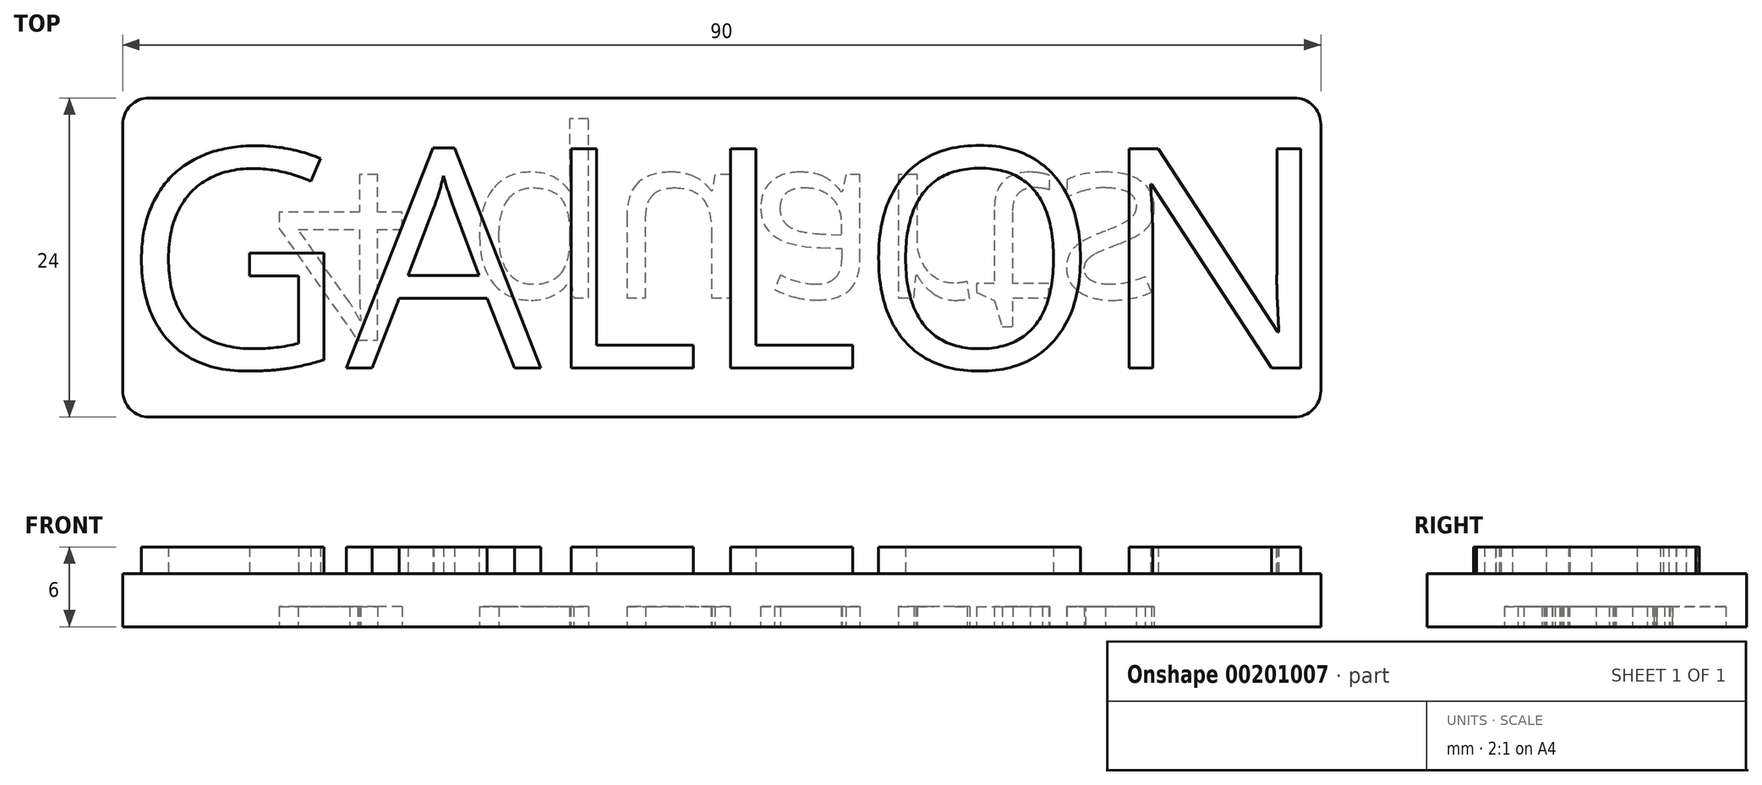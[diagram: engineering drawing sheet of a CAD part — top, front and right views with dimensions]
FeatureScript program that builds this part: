
annotation { "Feature Type Name" : "Feature", "Feature Type Description" : "" }
export const myFeature = defineFeature(function(context is Context, id is Id, definition is map)
    precondition{}
    {
        {
            var Q0;
            Q0=qCreatedBy(makeId("Top.planeOp"),FACE);
            var sketch = newSketch(context, id + "F0", { "sketchPlane" : qUnion([Q0])});
            skLineSegment(sketch, "E0.bottom", {"start": v(-45, 12) * mm, "end": v(45, 12) * mm});
            skLineSegment(sketch, "E0.top", {"start": v(-45, -12) * mm, "end": v(45, -12) * mm});
            skLineSegment(sketch, "E0.left", {"start": v(-45, 12) * mm, "end": v(-45, -12) * mm});
            skLineSegment(sketch, "E0.right", {"start": v(45, 12) * mm, "end": v(45, -12) * mm});
            skLineSegment(sketch, "E1", {"start": v(0, -12) * mm, "end": v(0, 12) * mm, "construction": true});
            skSolve(sketch);
        }
        {
            var Q0;
            Q0=makeQuery(id+"F0.imprint","IMPRINT",FACE,{"disambiguationData":[TD([[makeQuery(id+"F0.imprint","IMPRINT",EDGE,{"derivedFrom":sQuery(id+"F0.wireOp",EDGE,"E0.bottom")}),-1.0]])]});
            extrude(context, id + "F1", {"entities" : qUnion([Q0]), "depth" : 4 * mm});
        }
        {
            var Q0;
            Q0=makeQuery(id+"F1.opExtrude","SWEPT_EDGE",EDGE,{"disambiguationData":[OSD([sQuery(id+"F0.wireOp",EDGE,"E0.top"),sQuery(id+"F0.wireOp",EDGE,"E0.left")])]});
            var Q1;
            Q1=makeQuery(id+"F1.opExtrude","SWEPT_EDGE",EDGE,{"disambiguationData":[OSD([sQuery(id+"F0.wireOp",EDGE,"E0.bottom"),sQuery(id+"F0.wireOp",EDGE,"E0.right")])]});
            var Q2;
            Q2=makeQuery(id+"F1.opExtrude","SWEPT_EDGE",EDGE,{"disambiguationData":[OSD([sQuery(id+"F0.wireOp",EDGE,"E0.bottom"),sQuery(id+"F0.wireOp",EDGE,"E0.left")])]});
            var Q3;
            Q3=makeQuery(id+"F1.opExtrude","SWEPT_EDGE",EDGE,{"disambiguationData":[OSD([sQuery(id+"F0.wireOp",EDGE,"E0.top"),sQuery(id+"F0.wireOp",EDGE,"E0.right")])]});
            fillet(context, id + "F2", {"entities" : qUnion([Q0, Q1, Q2, Q3]), "radius" : 2 * mm, "tangentPropagation" : true, "allowEdgeOverflow" : false});
        }
        {
            var Q0;
            Q0=makeQuery(id+"F1.opExtrude","CAP_FACE",FACE,{"disambiguationData":[OSD([sQuery(id+"F0.wireOp",EDGE,"E0.bottom"),sQuery(id+"F0.wireOp",EDGE,"E0.top"),sQuery(id+"F0.wireOp",EDGE,"E0.left"),sQuery(id+"F0.wireOp",EDGE,"E0.right")])],"isStart":false});
            var sketch = newSketch(context, id + "F3", { "sketchPlane" : qUnion([Q0])});
            skText(sketch, "E2", { "text": "GALLON", "fontName": "OpenSans-Regular.ttf"});
            const initialGuessF3  = {"E2": [-0.045, -0.00831, 1, 0, 0.01662]};
            skSetInitialGuess(sketch, initialGuessF3);
            skSolve(sketch);
        }
        {
            var Q0;
            {var subQ0=sQuery(id+"F3.wireOp",EDGE,"E2.sketch_text.stroke-4");Q0=makeQuery(id+"F3.imprint","IMPRINT",FACE,{"disambiguationData":[TD([[makeQuery(id+"F3.imprint","IMPRINT",EDGE,{"derivedFrom":subQ0}),-1.0]])]});}
            var Q1;
            {var subQ0=sQuery(id+"F3.wireOp",EDGE,"E2.sketch_text.stroke-3");var subQ1=sQuery(id+"F3.wireOp",EDGE,"E2.sketch_text.stroke-2");var subQ2=makeQuery(id+"F3.imprint","INTERSECT",VERTEX,{"derivedFrom":[subQ1,subQ0]});Q1=makeQuery(id+"F3.imprint","IMPRINT",FACE,{"disambiguationData":[TD([[makeQuery(id+"F3.imprint","IMPRINT",EDGE,{"disambiguationData":[TD([[subQ2,1.0]])],"derivedFrom":subQ1}),-1.0]])]});}
            var Q2;
            {var subQ1=sQuery(id+"F3.wireOp",EDGE,"E2.sketch_text.stroke-1");Q2=makeQuery(id+"F3.imprint","IMPRINT",FACE,{"disambiguationData":[TD([[makeQuery(id+"F3.imprint","IMPRINT",EDGE,{"derivedFrom":subQ1}),-1.0]])]});}
            var Q3;
            {var subQ0=sQuery(id+"F3.wireOp",EDGE,"E2.sketch_text.stroke-0");var subQ1=makeQuery(id+"F1.opExtrude","CAP_EDGE",EDGE,{"disambiguationData":[OSD([sQuery(id+"F0.wireOp",EDGE,"E0.top")])],"isStart":false});var subQ2=makeQuery(id+"F3.imprint","INTERSECT",VERTEX,{"derivedFrom":[subQ1,subQ0]});Q3=makeQuery(id+"F3.imprint","IMPRINT",FACE,{"disambiguationData":[TD([[makeQuery(id+"F3.imprint","IMPRINT",EDGE,{"disambiguationData":[TD([[subQ2,-1.0]])],"derivedFrom":subQ0}),-1.0]])]});}
            var Q4;
            {var subQ1=sQuery(id+"F3.wireOp",EDGE,"E2.sketch_text.stroke-8");Q4=makeQuery(id+"F3.imprint","IMPRINT",FACE,{"disambiguationData":[TD([[makeQuery(id+"F3.imprint","IMPRINT",EDGE,{"derivedFrom":subQ1}),-1.0]])]});}
            var Q5;
            {var subQ0=sQuery(id+"F3.wireOp",EDGE,"E2.sketch_text.stroke-9");var subQ1=makeQuery(id+"F1.opExtrude","CAP_EDGE",EDGE,{"disambiguationData":[OSD([sQuery(id+"F0.wireOp",EDGE,"E0.bottom")])],"isStart":false});var subQ2=makeQuery(id+"F3.imprint","INTERSECT",VERTEX,{"derivedFrom":[subQ1,subQ0]});Q5=makeQuery(id+"F3.imprint","IMPRINT",FACE,{"disambiguationData":[TD([[makeQuery(id+"F3.imprint","IMPRINT",EDGE,{"disambiguationData":[TD([[subQ2,1.0]])],"derivedFrom":subQ0}),-1.0]])]});}
            var Q6;
            {var subQ1=sQuery(id+"F3.wireOp",EDGE,"E2.sketch_text.stroke-10");Q6=makeQuery(id+"F3.imprint","IMPRINT",FACE,{"disambiguationData":[TD([[makeQuery(id+"F3.imprint","IMPRINT",EDGE,{"derivedFrom":subQ1}),-1.0]])]});}
            var Q7;
            {var subQ0=sQuery(id+"F3.wireOp",EDGE,"E2.sketch_text.stroke-11");var subQ1=makeQuery(id+"F1.opExtrude","CAP_EDGE",EDGE,{"disambiguationData":[OSD([sQuery(id+"F0.wireOp",EDGE,"E0.bottom")])],"isStart":false});var subQ2=makeQuery(id+"F3.imprint","INTERSECT",VERTEX,{"derivedFrom":[subQ1,subQ0]});Q7=makeQuery(id+"F3.imprint","IMPRINT",FACE,{"disambiguationData":[TD([[makeQuery(id+"F3.imprint","IMPRINT",EDGE,{"disambiguationData":[TD([[subQ2,-1.0]])],"derivedFrom":subQ0}),-1.0]])]});}
            var Q8;
            {var subQ0=sQuery(id+"F3.wireOp",EDGE,"E2.sketch_text.stroke-12");Q8=makeQuery(id+"F3.imprint","IMPRINT",FACE,{"disambiguationData":[TD([[makeQuery(id+"F3.imprint","IMPRINT",EDGE,{"derivedFrom":subQ0}),-1.0]])]});}
            var Q9;
            {var subQ0=sQuery(id+"F3.wireOp",EDGE,"E2.sketch_text.stroke-21");Q9=makeQuery(id+"F3.imprint","IMPRINT",FACE,{"disambiguationData":[TD([[makeQuery(id+"F3.imprint","IMPRINT",EDGE,{"derivedFrom":subQ0}),-1.0]])]});}
            var Q10;
            {var subQ0=sQuery(id+"F3.wireOp",EDGE,"E2.sketch_text.stroke-18");var subQ1=makeQuery(id+"F1.opExtrude","CAP_EDGE",EDGE,{"disambiguationData":[OSD([sQuery(id+"F0.wireOp",EDGE,"E0.top")])],"isStart":false});var subQ2=makeQuery(id+"F3.imprint","INTERSECT",VERTEX,{"derivedFrom":[subQ1,subQ0]});Q10=makeQuery(id+"F3.imprint","IMPRINT",FACE,{"disambiguationData":[TD([[makeQuery(id+"F3.imprint","IMPRINT",EDGE,{"disambiguationData":[TD([[subQ2,-1.0]])],"derivedFrom":subQ0}),-1.0]])]});}
            var Q11;
            {var subQ0=sQuery(id+"F3.wireOp",EDGE,"E2.sketch_text.stroke-19");Q11=makeQuery(id+"F3.imprint","IMPRINT",FACE,{"disambiguationData":[TD([[makeQuery(id+"F3.imprint","IMPRINT",EDGE,{"derivedFrom":subQ0}),-1.0]])]});}
            var Q12;
            {var subQ0=sQuery(id+"F3.wireOp",EDGE,"E2.sketch_text.stroke-25");Q12=makeQuery(id+"F3.imprint","IMPRINT",FACE,{"disambiguationData":[TD([[makeQuery(id+"F3.imprint","IMPRINT",EDGE,{"derivedFrom":subQ0}),-1.0]])]});}
            var Q13;
            {var subQ0=sQuery(id+"F3.wireOp",EDGE,"E2.sketch_text.stroke-22");var subQ1=makeQuery(id+"F1.opExtrude","CAP_EDGE",EDGE,{"disambiguationData":[OSD([sQuery(id+"F0.wireOp",EDGE,"E0.top")])],"isStart":false});var subQ2=makeQuery(id+"F3.imprint","INTERSECT",VERTEX,{"derivedFrom":[subQ1,subQ0]});Q13=makeQuery(id+"F3.imprint","IMPRINT",FACE,{"disambiguationData":[TD([[makeQuery(id+"F3.imprint","IMPRINT",EDGE,{"disambiguationData":[TD([[subQ2,-1.0]])],"derivedFrom":subQ0}),-1.0]])]});}
            var Q14;
            {var subQ0=sQuery(id+"F3.wireOp",EDGE,"E2.sketch_text.stroke-23");Q14=makeQuery(id+"F3.imprint","IMPRINT",FACE,{"disambiguationData":[TD([[makeQuery(id+"F3.imprint","IMPRINT",EDGE,{"derivedFrom":subQ0}),-1.0]])]});}
            var Q15;
            {var subQ5=sQuery(id+"F3.wireOp",EDGE,"E2.sketch_text.stroke-28");Q15=makeQuery(id+"F3.imprint","IMPRINT",FACE,{"disambiguationData":[TD([[makeQuery(id+"F3.imprint","IMPRINT",EDGE,{"derivedFrom":subQ5}),-1.0]])]});}
            var Q16;
            {var subQ0=sQuery(id+"F3.wireOp",EDGE,"E2.sketch_text.stroke-34");Q16=makeQuery(id+"F3.imprint","IMPRINT",FACE,{"disambiguationData":[TD([[makeQuery(id+"F3.imprint","IMPRINT",EDGE,{"derivedFrom":subQ0}),-1.0]])]});}
            var Q17;
            {var subQ0=sQuery(id+"F3.wireOp",EDGE,"E2.sketch_text.stroke-30");Q17=makeQuery(id+"F3.imprint","IMPRINT",FACE,{"disambiguationData":[TD([[makeQuery(id+"F3.imprint","IMPRINT",EDGE,{"derivedFrom":subQ0}),-1.0]])]});}
            var Q18;
            {var subQ0=sQuery(id+"F3.wireOp",EDGE,"E2.sketch_text.stroke-6");Q18=makeQuery(id+"F3.imprint","IMPRINT",FACE,{"disambiguationData":[TD([[makeQuery(id+"F3.imprint","IMPRINT",EDGE,{"derivedFrom":subQ0}),-1.0]])]});}
            var Q19;
            {var subQ0=sQuery(id+"F3.wireOp",EDGE,"E2.sketch_text.stroke-17");Q19=makeQuery(id+"F3.imprint","IMPRINT",FACE,{"disambiguationData":[TD([[makeQuery(id+"F3.imprint","IMPRINT",EDGE,{"derivedFrom":subQ0}),-1.0]])]});}
            var Q20;
            {var subQ0=sQuery(id+"F3.wireOp",EDGE,"E2.sketch_text.stroke-27");Q20=makeQuery(id+"F3.imprint","IMPRINT",FACE,{"disambiguationData":[TD([[makeQuery(id+"F3.imprint","IMPRINT",EDGE,{"derivedFrom":subQ0}),-1.0]])]});}
            var Q21;
            Q21=makeQuery(id+"F3.imprint","IMPRINT",FACE,{"disambiguationData":[TD([[makeQuery(id+"F3.imprint","IMPRINT",EDGE,{"derivedFrom":sQuery(id+"F3.wireOp",EDGE,"E2.sketch_text.stroke-39")}),-1.0]])]});
            var Q22;
            Q22=makeQuery(id+"F3.imprint","IMPRINT",FACE,{"disambiguationData":[TD([[makeQuery(id+"F3.imprint","IMPRINT",EDGE,{"derivedFrom":sQuery(id+"F3.wireOp",EDGE,"E2.sketch_text.stroke-45")}),-1.0]])]});
            var Q23;
            Q23=makeQuery(id+"F3.imprint","IMPRINT",FACE,{"disambiguationData":[TD([[makeQuery(id+"F3.imprint","IMPRINT",EDGE,{"derivedFrom":sQuery(id+"F3.wireOp",EDGE,"E2.sketch_text.stroke-61")}),-1.0]])]});
            extrude(context, id + "F4", {"entities" : qUnion([Q0, Q1, Q2, Q3, Q4, Q5, Q6, Q7, Q8, Q9, Q10, Q11, Q12, Q13, Q14, Q15, Q16, Q17, Q18, Q19, Q20, Q21, Q22, Q23]), "operationType" : NewBodyOperationType.ADD, "depth" : 2 * mm});
        }
        {
            var Q0;
            Q0=makeQuery(id+"F1.opExtrude","CAP_FACE",FACE,{"disambiguationData":[OSD([sQuery(id+"F0.wireOp",EDGE,"E0.bottom"),sQuery(id+"F0.wireOp",EDGE,"E0.top"),sQuery(id+"F0.wireOp",EDGE,"E0.left"),sQuery(id+"F0.wireOp",EDGE,"E0.right")])],"isStart":true});
            var sketch = newSketch(context, id + "F5", { "sketchPlane" : qUnion([Q0])});
            skText(sketch, "E3", { "text": "4 quarts", "fontName": "OpenSans-Regular.ttf"});
            const initialGuessF5  = {"E3": [-0.0336, -0.00625, 1, 0, 0.0125]};
            skSetInitialGuess(sketch, initialGuessF5);
            skSolve(sketch);
        }
        {
            var Q0;
            Q0=makeQuery(id+"F5.imprint","IMPRINT",FACE,{"disambiguationData":[TD([[makeQuery(id+"F5.imprint","IMPRINT",EDGE,{"derivedFrom":sQuery(id+"F5.wireOp",EDGE,"E3.sketch_text.stroke-122")}),-1.0]])]});
            var Q1;
            Q1=makeQuery(id+"F5.imprint","IMPRINT",FACE,{"disambiguationData":[TD([[makeQuery(id+"F5.imprint","IMPRINT",EDGE,{"derivedFrom":sQuery(id+"F5.wireOp",EDGE,"E3.sketch_text.stroke-103")}),-1.0]])]});
            var Q2;
            Q2=makeQuery(id+"F5.imprint","IMPRINT",FACE,{"disambiguationData":[TD([[makeQuery(id+"F5.imprint","IMPRINT",EDGE,{"derivedFrom":sQuery(id+"F5.wireOp",EDGE,"E3.sketch_text.stroke-86")}),-1.0]])]});
            var Q3;
            Q3=makeQuery(id+"F5.imprint","IMPRINT",FACE,{"disambiguationData":[TD([[makeQuery(id+"F5.imprint","IMPRINT",EDGE,{"derivedFrom":sQuery(id+"F5.wireOp",EDGE,"E3.sketch_text.stroke-70")}),-1.0]])]});
            var Q4;
            Q4=makeQuery(id+"F5.imprint","IMPRINT",FACE,{"disambiguationData":[TD([[makeQuery(id+"F5.imprint","IMPRINT",EDGE,{"derivedFrom":sQuery(id+"F5.wireOp",EDGE,"E3.sketch_text.stroke-39")}),-1.0]])]});
            var Q5;
            Q5=makeQuery(id+"F5.imprint","IMPRINT",FACE,{"disambiguationData":[TD([[makeQuery(id+"F5.imprint","IMPRINT",EDGE,{"derivedFrom":sQuery(id+"F5.wireOp",EDGE,"E3.sketch_text.stroke-19")}),-1.0]])]});
            var Q6;
            Q6=makeQuery(id+"F5.imprint","IMPRINT",FACE,{"disambiguationData":[TD([[makeQuery(id+"F5.imprint","IMPRINT",EDGE,{"derivedFrom":sQuery(id+"F5.wireOp",EDGE,"E3.sketch_text.stroke-0")}),-1.0]])]});
            var Q7;
            Q7=makeQuery(id+"F5.imprint","IMPRINT",FACE,{"disambiguationData":[TD([[makeQuery(id+"F5.imprint","IMPRINT",EDGE,{"derivedFrom":sQuery(id+"F5.wireOp",EDGE,"E3.sketch_text.stroke-40")}),-1.0]])]});
            extrude(context, id + "F6", {"entities" : qUnion([Q0, Q1, Q2, Q3, Q4, Q5, Q6, Q7]), "operationType" : NewBodyOperationType.REMOVE, "oppositeDirection" : true, "depth" : 1.5 * mm});
        }
    });
